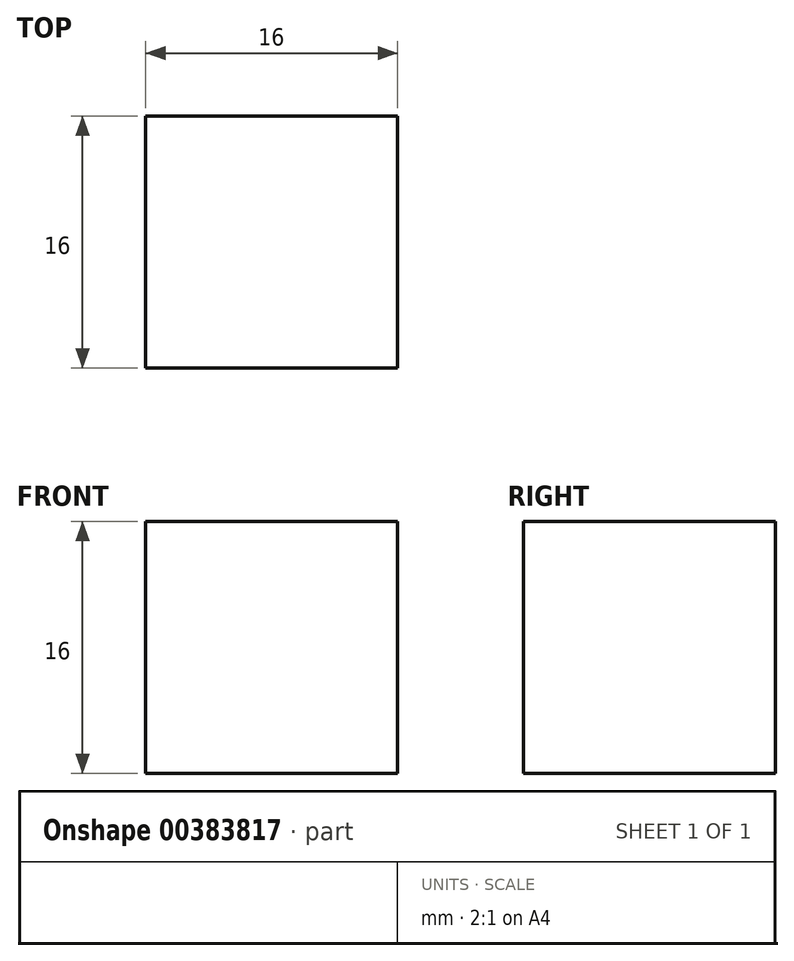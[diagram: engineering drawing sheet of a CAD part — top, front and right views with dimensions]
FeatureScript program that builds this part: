
annotation { "Feature Type Name" : "Feature", "Feature Type Description" : "" }
export const myFeature = defineFeature(function(context is Context, id is Id, definition is map)
    precondition{}
    {
        {
            var Q0;
            Q0=qCreatedBy(makeId("Top.planeOp"),FACE);
            var sketch = newSketch(context, id + "F0", { "sketchPlane" : qUnion([Q0])});
            skLineSegment(sketch, "E0.bottom", {"start": v(8, 8) * mm, "end": v(-8, 8) * mm});
            skLineSegment(sketch, "E0.top", {"start": v(8, -8) * mm, "end": v(-8, -8) * mm});
            skLineSegment(sketch, "E0.left", {"start": v(8, 8) * mm, "end": v(8, -8) * mm});
            skLineSegment(sketch, "E0.right", {"start": v(-8, 8) * mm, "end": v(-8, -8) * mm});
            skPoint(sketch, "E0.middle", {"position": v(0, 0) * mm});
            skSolve(sketch);
        }
        {
            var Q0;
            Q0 = qSketchRegion(id + "F0", true);
            extrude(context, id + "F1", {"entities" : qUnion([Q0]), "depth" : 16 * mm, "offsetDistance" : 25 * mm});
        }
    });
